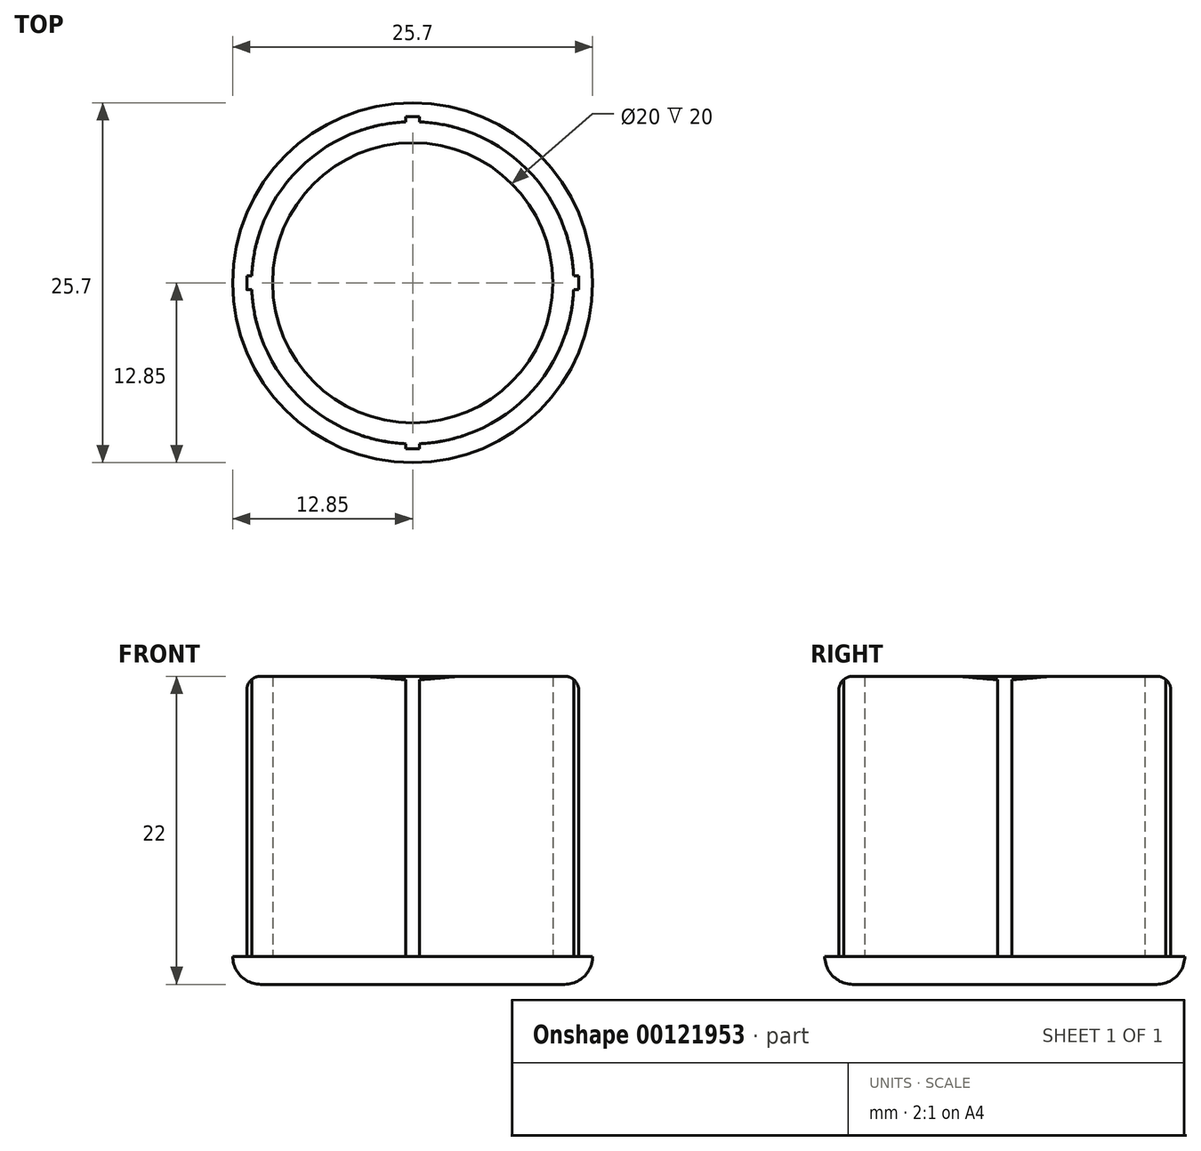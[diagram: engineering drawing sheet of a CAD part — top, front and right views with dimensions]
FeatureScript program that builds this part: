
annotation { "Feature Type Name" : "Feature", "Feature Type Description" : "" }
export const myFeature = defineFeature(function(context is Context, id is Id, definition is map)
    precondition{}
    {
        {
            var Q0;
            Q0=qCreatedBy(makeId("Top.planeOp"),FACE);
            var sketch = newSketch(context, id + "F0", { "sketchPlane" : qUnion([Q0])});
            skCircle(sketch, "E0", {"center": v(0, 0) * mm, "radius": 12.85 * mm});
            skSolve(sketch);
        }
        {
            var Q0;
            Q0=makeQuery(id+"F0.imprint","IMPRINT",FACE,{"disambiguationData":[TD([[makeQuery(id+"F0.imprint","IMPRINT",EDGE,{"derivedFrom":sQuery(id+"F0.wireOp",EDGE,"E0")}),1.0]])]});
            extrude(context, id + "F1", {"entities" : qUnion([Q0]), "depth" : 2 * mm});
        }
        {
            var Q0;
            Q0=makeQuery(id+"F1.opExtrude","CAP_FACE",FACE,{"disambiguationData":[OSD([sQuery(id+"F0.wireOp",EDGE,"E0")])],"isStart":false});
            var sketch = newSketch(context, id + "F2", { "sketchPlane" : qUnion([Q0])});
            skCircle(sketch, "E1", {"center": v(0, 0) * mm, "radius": 11.5 * mm});
            skLineSegment(sketch, "E2.bottom", {"start": v(0.5, -11.85) * mm, "end": v(-0.5, -11.85) * mm});
            skLineSegment(sketch, "E2.top", {"start": v(0.5, 11.85) * mm, "end": v(-0.5, 11.85) * mm});
            skLineSegment(sketch, "E2.left", {"start": v(0.5, -11.85) * mm, "end": v(0.5, 11.85) * mm});
            skLineSegment(sketch, "E2.right", {"start": v(-0.5, -11.85) * mm, "end": v(-0.5, 11.85) * mm});
            skLineSegment(sketch, "E3.bottom", {"start": v(11.85, -0.5) * mm, "end": v(-11.85, -0.5) * mm});
            skLineSegment(sketch, "E3.top", {"start": v(11.85, 0.5) * mm, "end": v(-11.85, 0.5) * mm});
            skLineSegment(sketch, "E3.left", {"start": v(11.85, -0.5) * mm, "end": v(11.85, 0.5) * mm});
            skLineSegment(sketch, "E3.right", {"start": v(-11.85, -0.5) * mm, "end": v(-11.85, 0.5) * mm});
            skCircle(sketch, "E4", {"center": v(0, 0) * mm, "radius": 10 * mm});
            skSolve(sketch);
        }
        {
            var Q0;
            Q0 = qSketchRegion(id + "F2", true);
            extrude(context, id + "F3", {"entities" : qUnion([Q0]), "operationType" : NewBodyOperationType.ADD, "depth" : 20 * mm});
        }
        {
            var Q0;
            Q0=makeQuery(id+"F3.opExtrude","CAP_EDGE",EDGE,{"disambiguationData":[OSD([sQuery(id+"F2.wireOp",EDGE,"E3.left")])],"isStart":false});
            var Q1;
            Q1=makeQuery(id+"F3.opExtrude","CAP_EDGE",EDGE,{"disambiguationData":[OSD([sQuery(id+"F2.wireOp",EDGE,"E2.top")])],"isStart":false});
            var Q2;
            Q2=makeQuery(id+"F3.opExtrude","CAP_EDGE",EDGE,{"disambiguationData":[OSD([sQuery(id+"F2.wireOp",EDGE,"E3.right")])],"isStart":false});
            var Q3;
            Q3=makeQuery(id+"F3.opExtrude","CAP_EDGE",EDGE,{"disambiguationData":[OSD([sQuery(id+"F2.wireOp",EDGE,"E2.bottom")])],"isStart":false});
            fillet(context, id + "F4", {"entities" : qUnion([Q0, Q1, Q2, Q3]), "radius" : 1 * mm, "tangentPropagation" : true, "allowEdgeOverflow" : false});
        }
        {
            var Q0;
            Q0=makeQuery(id+"F1.opExtrude","CAP_EDGE",EDGE,{"disambiguationData":[OSD([sQuery(id+"F0.wireOp",EDGE,"E0")])],"isStart":true});
            fillet(context, id + "F5", {"entities" : qUnion([Q0]), "radius" : 2 * mm, "tangentPropagation" : true, "allowEdgeOverflow" : false});
        }
    });
